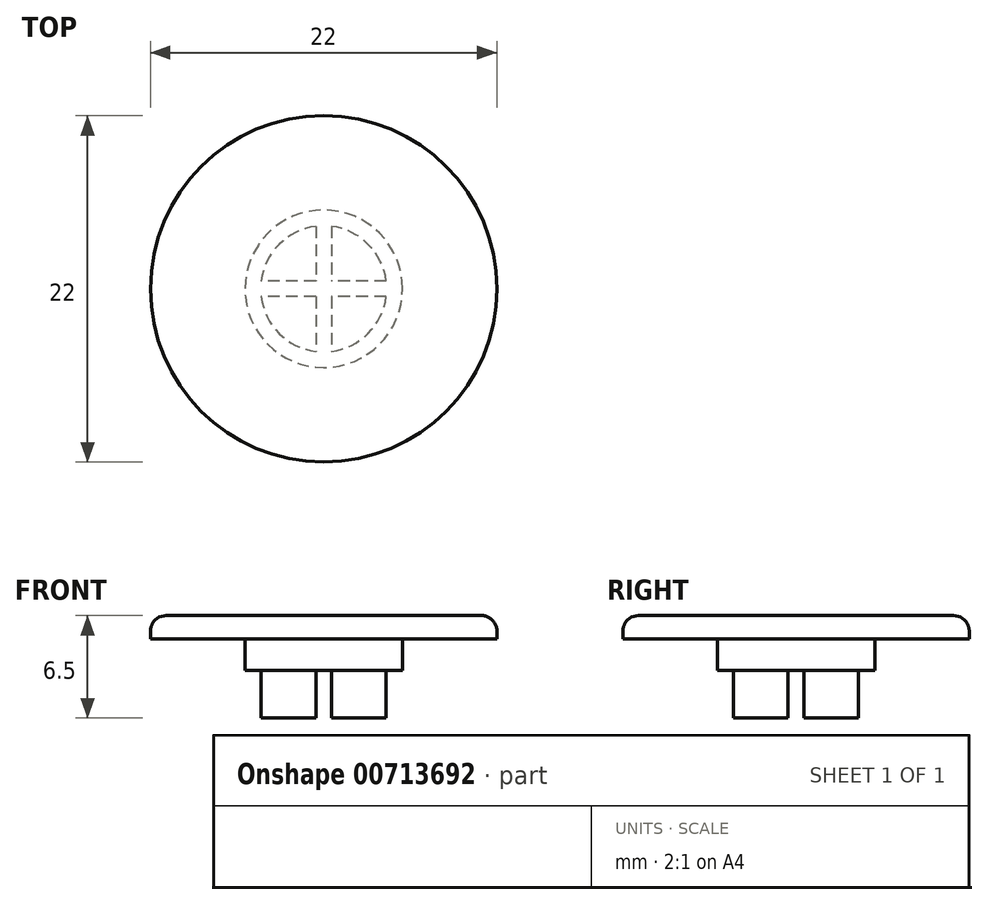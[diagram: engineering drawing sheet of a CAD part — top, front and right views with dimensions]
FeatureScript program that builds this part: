
annotation { "Feature Type Name" : "Feature", "Feature Type Description" : "" }
export const myFeature = defineFeature(function(context is Context, id is Id, definition is map)
    precondition{}
    {
        {
            var Q0;
            Q0=qCreatedBy(makeId("Front.planeOp"),FACE);
            var sketch = newSketch(context, id + "F0", { "sketchPlane" : qUnion([Q0])});
            skLineSegment(sketch, "E0", {"start": v(0, 0) * mm, "end": v(4, 0) * mm});
            skLineSegment(sketch, "E1", {"start": v(4, 0) * mm, "end": v(4, 3) * mm});
            skLineSegment(sketch, "E2", {"start": v(4, 3) * mm, "end": v(5, 3) * mm});
            skLineSegment(sketch, "E3", {"start": v(5, 3) * mm, "end": v(5, 5) * mm});
            skLineSegment(sketch, "E4", {"start": v(5, 5) * mm, "end": v(11, 5) * mm});
            skLineSegment(sketch, "E5", {"start": v(11, 5) * mm, "end": v(11, 6.5) * mm});
            skLineSegment(sketch, "E6", {"start": v(11, 6.5) * mm, "end": v(0, 6.5) * mm});
            skLineSegment(sketch, "E7", {"start": v(0, 6.5) * mm, "end": v(0, 0) * mm});
            skLineSegment(sketch, "E8", {"start": v(0, 0) * mm, "end": v(0, 10.6) * mm, "construction": true});
            skSolve(sketch);
        }
        {
            var Q0;
            Q0=qSketchRegion(id+"F0",true);
            var Q1;
            Q1=sQuery(id+"F0.wireOp",EDGE,"E8");
            revolve(context, id + "F1", {"surfaceOperationType" : NewSurfaceOperationType.NEW, "entities" : qUnion([Q0]), "axis" : qUnion([Q1]), "revolveType" : RevolveType.FULL});
        }
        {
            var Q0;
            Q0=makeQuery(id+"F1.opRevolve","SWEPT_FACE",FACE,{"disambiguationData":[OSD([sQuery(id+"F0.wireOp",EDGE,"E0")])]});
            var sketch = newSketch(context, id + "F2", { "sketchPlane" : qUnion([Q0])});
            skLineSegment(sketch, "E9.bottom", {"start": v(0.5, -6.4) * mm, "end": v(-0.5, -6.4) * mm});
            skLineSegment(sketch, "E9.top", {"start": v(0.5, 6.4) * mm, "end": v(-0.5, 6.4) * mm});
            skLineSegment(sketch, "E9.left", {"start": v(0.5, -6.4) * mm, "end": v(0.5, -0.5) * mm});
            skLineSegment(sketch, "E9.right", {"start": v(-0.5, -6.4) * mm, "end": v(-0.5, -0.5) * mm});
            skPoint(sketch, "E9.middle", {"position": v(0, 0) * mm});
            skLineSegment(sketch, "E10.bottom", {"start": v(5.62, -0.5) * mm, "end": v(0.5, -0.5) * mm});
            skLineSegment(sketch, "E10.top", {"start": v(5.62, 0.5) * mm, "end": v(0.5, 0.5) * mm});
            skLineSegment(sketch, "E10.left", {"start": v(5.62, -0.5) * mm, "end": v(5.62, 0.5) * mm});
            skLineSegment(sketch, "E10.right", {"start": v(-5.62, -0.5) * mm, "end": v(-5.62, 0.5) * mm});
            skLineSegment(sketch, "E11.trimOffspring", {"start": v(-0.5, 0.5) * mm, "end": v(-5.62, 0.5) * mm});
            skLineSegment(sketch, "E12.trimOffspring", {"start": v(0.5, 0.5) * mm, "end": v(0.5, 6.4) * mm});
            skLineSegment(sketch, "E13.trimOffspring", {"start": v(-0.5, -0.5) * mm, "end": v(-5.62, -0.5) * mm});
            skLineSegment(sketch, "E14.trimOffspring", {"start": v(-0.5, 0.5) * mm, "end": v(-0.5, 6.4) * mm});
            skSolve(sketch);
        }
        {
            var Q0;
            Q0=qSketchRegion(id+"F2",true);
            var Q1;
            Q1=makeQuery(id+"F1.opRevolve","SWEPT_FACE",FACE,{"disambiguationData":[OSD([sQuery(id+"F0.wireOp",EDGE,"E2")])]});
            extrude(context, id + "F3", {"entities" : qUnion([Q0]), "operationType" : NewBodyOperationType.REMOVE, "endBound" : BoundingType.UP_TO_SURFACE, "oppositeDirection" : true, "depth" : 25 * mm, "endBoundEntityFace" : qUnion([Q1]), "offsetDistance" : 25 * mm});
        }
        {
            var Q0;
            Q0=makeQuery(id+"F1.opRevolve","SWEPT_EDGE",EDGE,{"disambiguationData":[OSD([sQuery(id+"F0.wireOp",EDGE,"E5"),sQuery(id+"F0.wireOp",EDGE,"E6")])]});
            fillet(context, id + "F4", {"entities" : qUnion([Q0]), "radius" : 1 * mm, "tangentPropagation" : true, "allowEdgeOverflow" : false});
        }
    });
